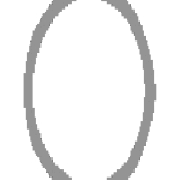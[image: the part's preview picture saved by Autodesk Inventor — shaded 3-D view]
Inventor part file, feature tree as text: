
AUTODESK INVENTOR PART (.ipt)
format: ipt  version: 2021 (Build 250183000, 183)  size: 109,568 bytes
history: native  units: in
note: dims shown in document units (in); Inventor stores cm internally (conversion verified against a paired STEP export)
features: other x4, sketch x3, plane x1
ambient origin geometry x8: Origin, YZ Plane, XZ Plane, XY Plane, X Axis, Y Axis, Z Axis, Center Point
bodies: Solid1 (feature_tree), Body (feature_tree)
feature tree (8):
  other  "Driven Length"
  other  "Frame Generator"
  other  "Start Plane"
  other  "End Plane"
  sketch  "Sketch"  dims[d2=13.5in d4=-0.0in d5=13.5in d6=0.12in d7=0.0in d8=90.0deg d9=13.5in]
  sketch  "Sketch2"  dims[d0=1.0in]
  plane  "Work Plane3"
  sketch  "Sketch3"  dims[d1=0.065in]
